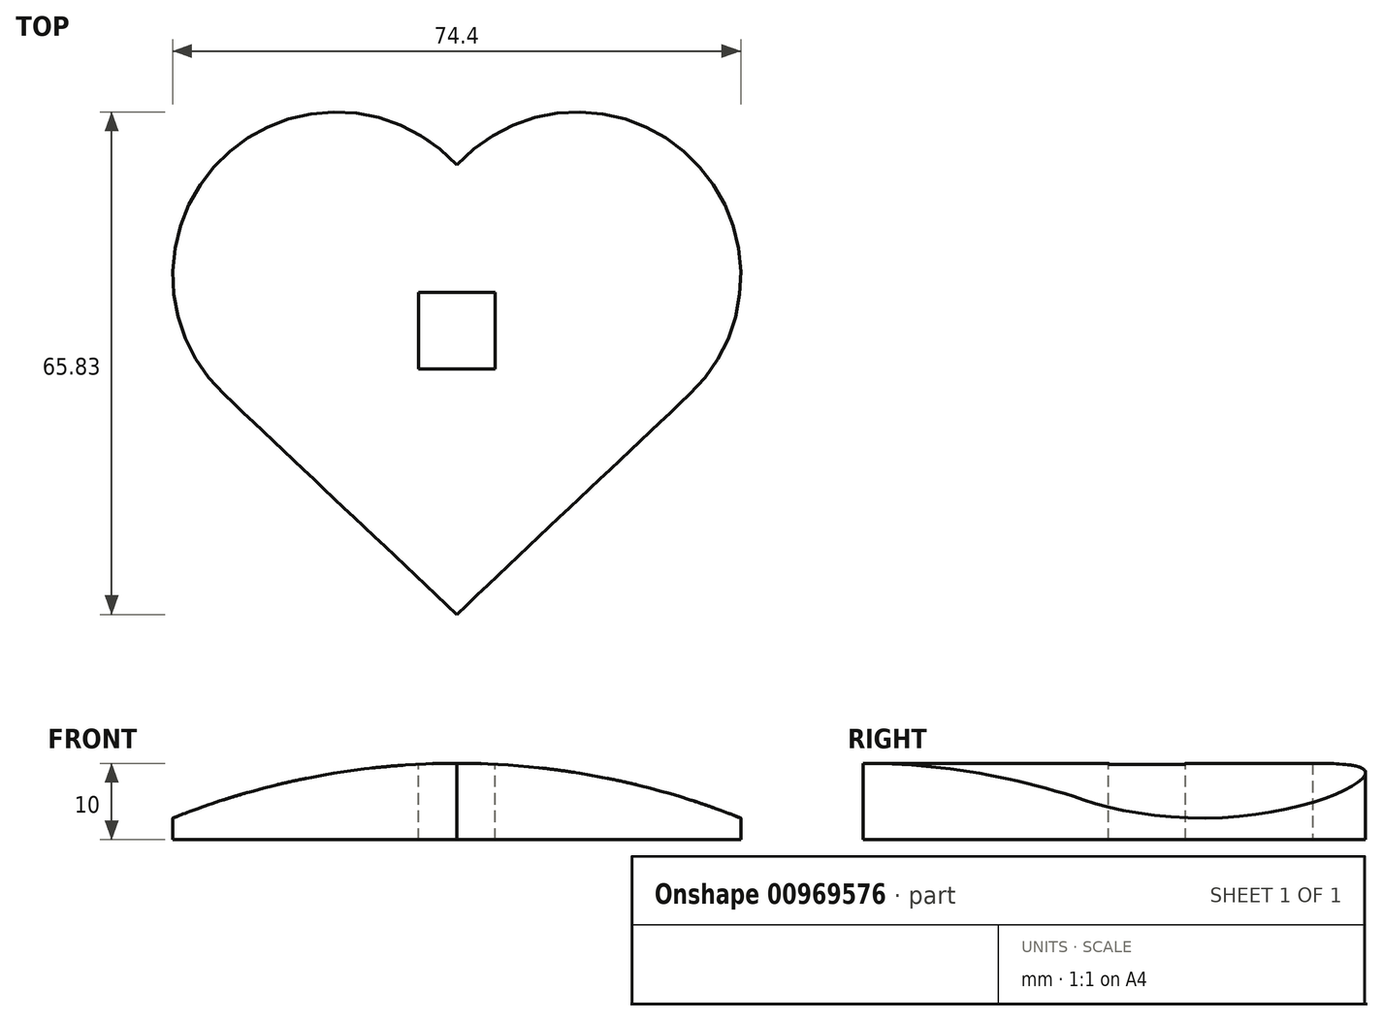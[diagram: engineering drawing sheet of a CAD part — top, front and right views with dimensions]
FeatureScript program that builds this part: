
annotation { "Feature Type Name" : "Feature", "Feature Type Description" : "" }
export const myFeature = defineFeature(function(context is Context, id is Id, definition is map)
    precondition{}
    {
        {
            var Q0;
            Q0=qCreatedBy(makeId("Top.planeOp"),FACE);
            var sketch = newSketch(context, id + "F0", { "sketchPlane" : qUnion([Q0])});
            skLineSegment(sketch, "E0", {"start": v(0, 0) * mm, "end": v(30.5, 28.85) * mm});
            skArc(sketch, "E1", {"start": v(30.5, 28.85) * mm, "mid": v(30.81, 59.67) * mm, "end": v(0, 58.9) * mm});
            skLineSegment(sketch, "E2", {"start": v(0, 0) * mm, "end": v(0, 58.9) * mm});
            skArc(sketch, "E3.MirrorCS", {"start": v(-30.5, 28.85) * mm, "mid": v(-30.81, 59.67) * mm, "end": v(0, 58.9) * mm});
            skLineSegment(sketch, "E4.MirrorCS", {"start": v(0, 0) * mm, "end": v(-30.5, 28.85) * mm});
            skSolve(sketch);
        }
        {
            var Q0;
            Q0=makeQuery(id+"F0.imprint","IMPRINT",FACE,{"disambiguationData":[TD([[makeQuery(id+"F0.imprint","IMPRINT",EDGE,{"derivedFrom":sQuery(id+"F0.wireOp",EDGE,"E2")}),1.0]])]});
            var Q1;
            Q1=makeQuery(id+"F0.imprint","IMPRINT",FACE,{"disambiguationData":[TD([[makeQuery(id+"F0.imprint","IMPRINT",EDGE,{"derivedFrom":sQuery(id+"F0.wireOp",EDGE,"E0")}),1.0]])]});
            extrude(context, id + "F1", {"entities" : qUnion([Q0, Q1]), "depth" : 10 * mm, "offsetDistance" : 25 * mm});
        }
        {
            var Q0;
            Q0=qCreatedBy(makeId("Front.planeOp"),FACE);
            var sketch = newSketch(context, id + "F2", { "sketchPlane" : qUnion([Q0])});
            skLineSegment(sketch, "E5", {"start": v(0, 0) * mm, "end": v(0, -90) * mm});
            skLineSegment(sketch, "E6", {"start": v(0, 0) * mm, "end": v(0, 10) * mm});
            skCircle(sketch, "E7", {"center": v(0, -90) * mm, "radius": 100 * mm});
            skCircle(sketch, "E8", {"center": v(0, -90) * mm, "radius": 135.5 * mm});
            skSolve(sketch);
        }
        {
            var Q0;
            Q0=makeQuery(id+"F2.imprint","IMPRINT",FACE,{"disambiguationData":[TD([[makeQuery(id+"F2.imprint","IMPRINT",EDGE,{"derivedFrom":sQuery(id+"F2.wireOp",EDGE,"E7")}),-1.0]])]});
            extrude(context, id + "F3", {"entities" : qUnion([Q0]), "operationType" : NewBodyOperationType.REMOVE, "oppositeDirection" : true, "depth" : 134 * mm, "offsetDistance" : 25 * mm});
        }
        {
            var Q0;
            Q0=qCreatedBy(makeId("Top.planeOp"),FACE);
            var sketch = newSketch(context, id + "F4", { "sketchPlane" : qUnion([Q0])});
            skLineSegment(sketch, "E9.bottom", {"start": v(5.03, 42.23) * mm, "end": v(-5.03, 42.23) * mm});
            skLineSegment(sketch, "E9.top", {"start": v(5.03, 32.18) * mm, "end": v(-5.03, 32.18) * mm});
            skLineSegment(sketch, "E9.left", {"start": v(5.03, 42.23) * mm, "end": v(5.03, 32.18) * mm});
            skLineSegment(sketch, "E9.right", {"start": v(-5.03, 42.23) * mm, "end": v(-5.03, 32.18) * mm});
            skPoint(sketch, "E9.middle", {"position": v(0, 37.2) * mm});
            skSolve(sketch);
        }
        {
            var Q0;
            Q0 = qSketchRegion(id + "F4", true);
            extrude(context, id + "F5", {"entities" : qUnion([Q0]), "operationType" : NewBodyOperationType.REMOVE, "endBound" : BoundingType.SYMMETRIC, "oppositeDirection" : true, "depth" : 25 * mm, "offsetDistance" : 25 * mm});
        }
    });
